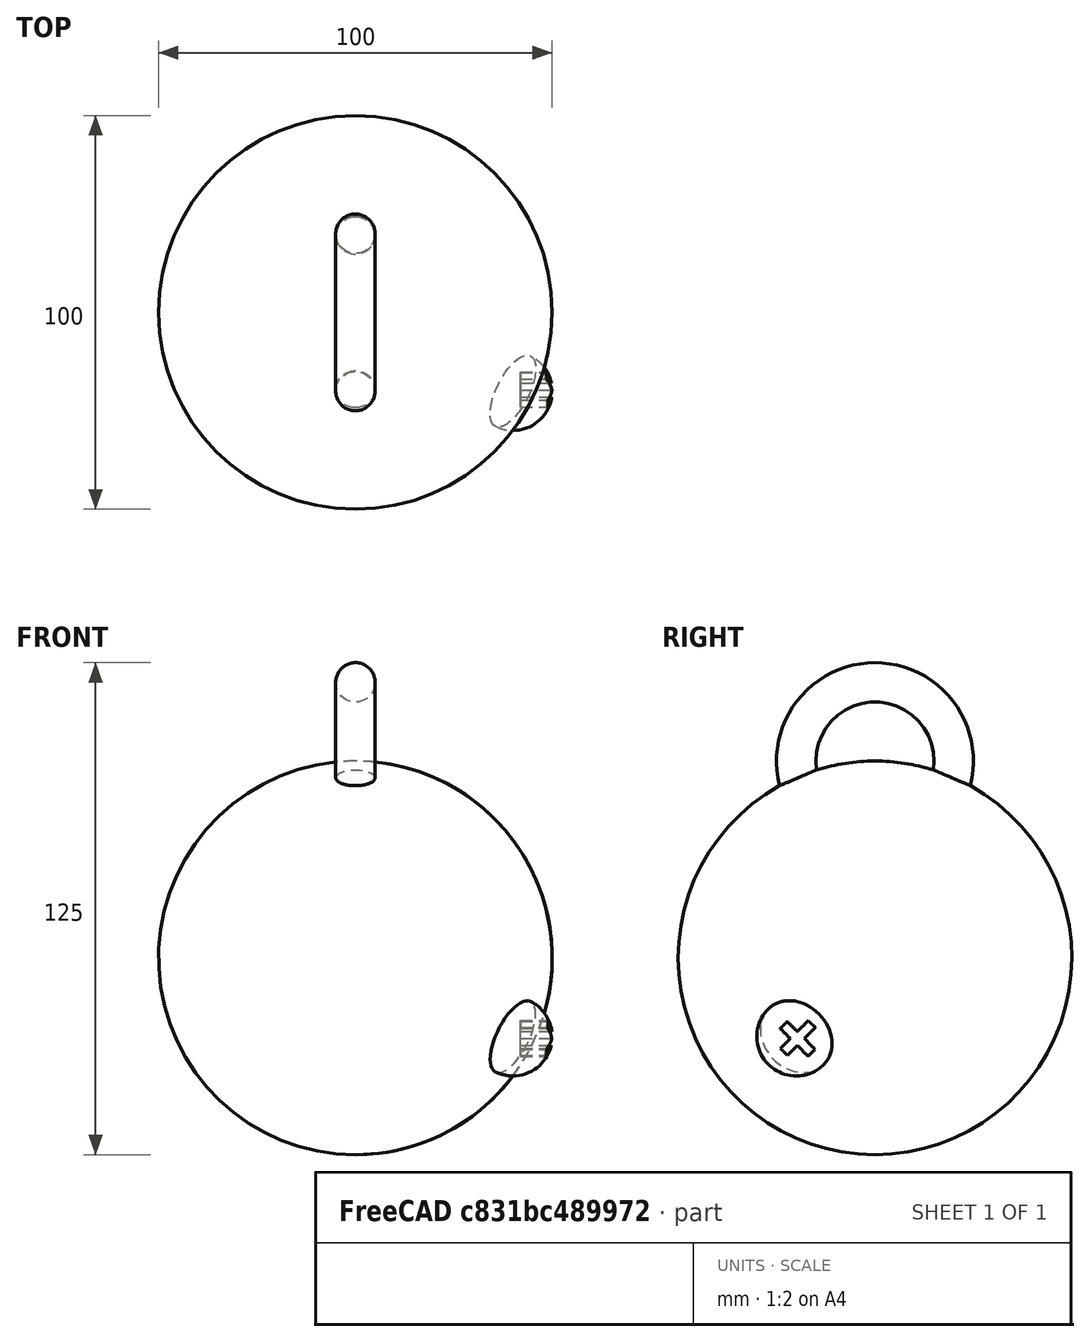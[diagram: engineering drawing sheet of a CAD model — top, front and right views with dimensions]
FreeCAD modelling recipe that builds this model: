
FCSTD DOCUMENT  (FreeCAD 0.16R6703 (Git))
Label: portecleventremoubosse
License: All rights reserved
LicenseURL: http://en.wikipedia.org/wiki/All_rights_reserved
objects: Part::Sphere×2, Part::Box×2, Part::MultiFuse×2, Part::Cut×2, Part::Torus×1
note: 9 computed .brp shape members not serialized (recipe doc carries the construction recipe); baked Part::Feature solids carry a one-line shape summary decoded from their .brp

FEATURE [Part::Sphere] Sphere  label="Sphère"
  Angle1 = -90
  Angle2 = 90
  Angle3 = 360
  Radius = 50
FEATURE [Part::Sphere] Sphere001  label="Sphère001"
  Angle1 = -90
  Angle2 = 90
  Angle3 = 360
  Placement = pos=(40,-20,-20) rot=(0,0,1;0rad)
  Radius = 10
FEATURE [Part::Box] Box  label="Boîte"
  Height = 10
  Length = 10
  Placement = pos=(42,-17,-25) rot=(1,0,0;0.785398rad)
  Width = 2.5
FEATURE [Part::Box] Box001  label="Boîte001"
  Height = 10
  Length = 10
  Placement = pos=(42,-24,-23) rot=(-1,0,0;0.785398rad)
  Width = 2.5
FEATURE [Part::Torus] Torus  label="Tore"
  Angle1 = -180
  Angle2 = 180
  Angle3 = 360
  Placement = pos=(0,0,50) rot=(0,1,0;1.5708rad)
  Radius1 = 20
  Radius2 = 5
FEATURE [Part::MultiFuse] Fusion
  Shapes = -> [Sphere,Sphere001]
FEATURE [Part::MultiFuse] Fusion001
  Shapes = -> [Fusion,Torus]
FEATURE [Part::Cut] Cut
  Base = -> Fusion001
  Tool = -> Box001
FEATURE [Part::Cut] Cut001
  Base = -> Cut
  Tool = -> Box
